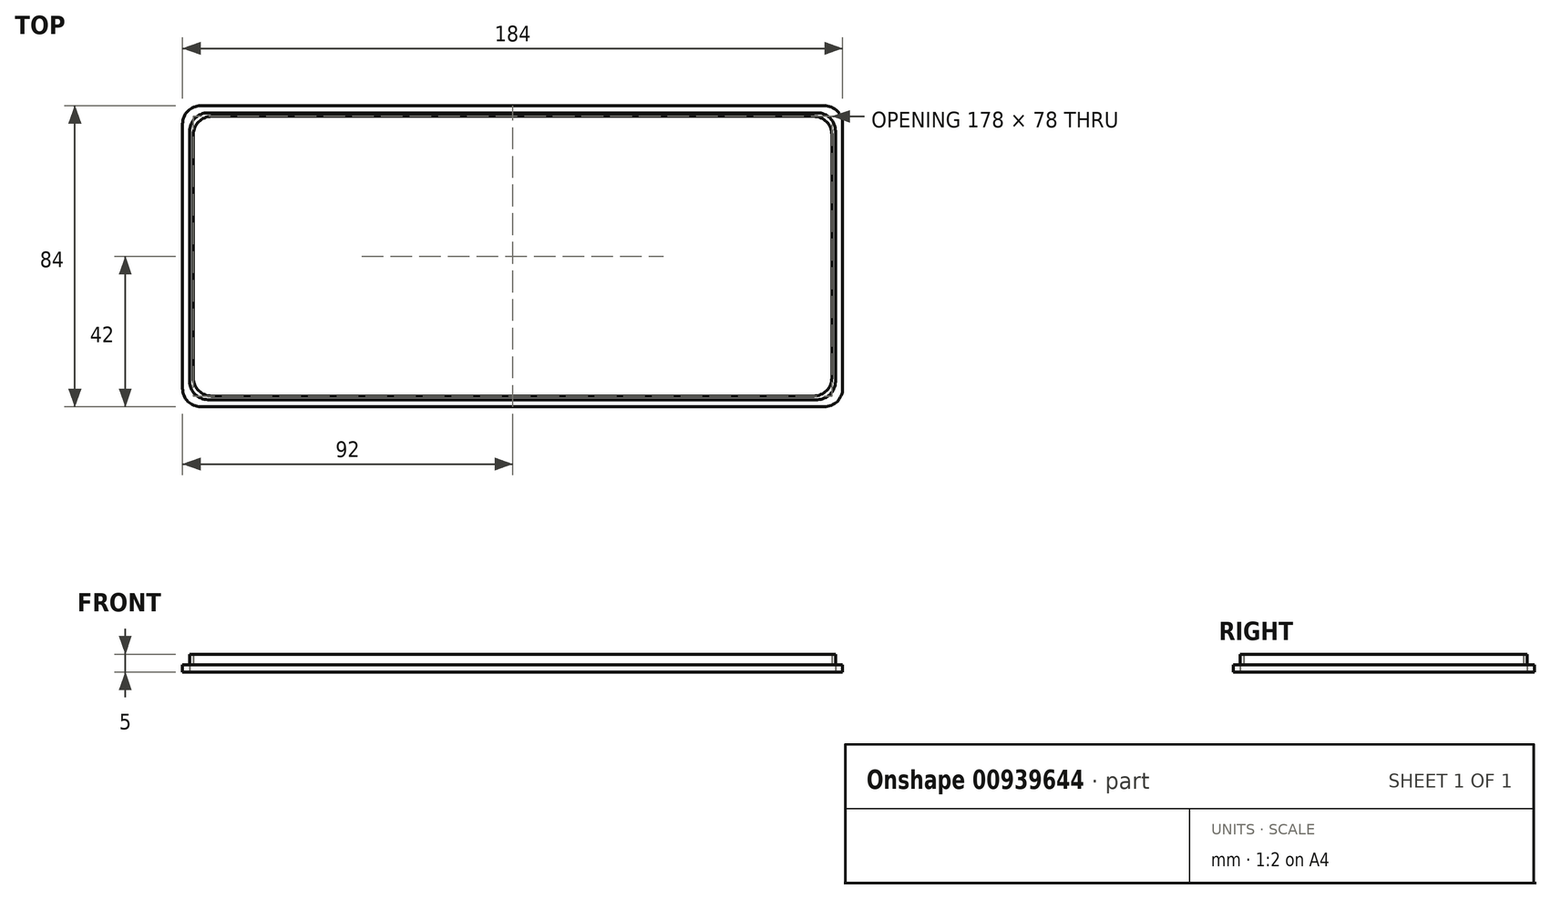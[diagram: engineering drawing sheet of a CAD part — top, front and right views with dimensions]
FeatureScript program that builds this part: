
annotation { "Feature Type Name" : "Feature", "Feature Type Description" : "" }
export const myFeature = defineFeature(function(context is Context, id is Id, definition is map)
    precondition{}
    {
        {
            var Q0;
            Q0=qCreatedBy(makeId("Top.planeOp"),FACE);
            var sketch = newSketch(context, id + "F0", { "sketchPlane" : qUnion([Q0])});
            skLineSegment(sketch, "E0.bottom", {"start": v(-90, 40) * mm, "end": v(90, 40) * mm});
            skLineSegment(sketch, "E0.top", {"start": v(-90, -40) * mm, "end": v(90, -40) * mm});
            skLineSegment(sketch, "E0.left", {"start": v(-90, 40) * mm, "end": v(-90, -40) * mm});
            skLineSegment(sketch, "E0.right", {"start": v(90, 40) * mm, "end": v(90, -40) * mm});
            skPoint(sketch, "E0.middle", {"position": v(0, 0) * mm});
            skLineSegment(sketch, "E1.0", {"start": v(-92, -42) * mm, "end": v(92, -42) * mm});
            skLineSegment(sketch, "E1.1", {"start": v(-92, 42) * mm, "end": v(-92, -42) * mm});
            skLineSegment(sketch, "E1.2", {"start": v(-92, 42) * mm, "end": v(92, 42) * mm});
            skLineSegment(sketch, "E1.3", {"start": v(92, 42) * mm, "end": v(92, -42) * mm});
            skLineSegment(sketch, "E2.bottom", {"start": v(-89, 39) * mm, "end": v(89, 39) * mm});
            skLineSegment(sketch, "E2.top", {"start": v(-89, -39) * mm, "end": v(89, -39) * mm});
            skLineSegment(sketch, "E2.left", {"start": v(-89, 39) * mm, "end": v(-89, -39) * mm});
            skLineSegment(sketch, "E2.right", {"start": v(89, 39) * mm, "end": v(89, -39) * mm});
            skSolve(sketch);
        }
        {
            var Q0;
            Q0=makeQuery(id+"F0.imprint","IMPRINT",FACE,{"disambiguationData":[TD([[makeQuery(id+"F0.imprint","IMPRINT",EDGE,{"derivedFrom":sQuery(id+"F0.wireOp",EDGE,"E0.bottom")}),1.0]])]});
            var Q1;
            Q1=makeQuery(id+"F0.imprint","IMPRINT",FACE,{"disambiguationData":[TD([[makeQuery(id+"F0.imprint","IMPRINT",EDGE,{"derivedFrom":sQuery(id+"F0.wireOp",EDGE,"E2.bottom")}),-1.0]])]});
            var Q2;
            Q2=makeQuery(id+"F0.imprint","IMPRINT",FACE,{"disambiguationData":[TD([[makeQuery(id+"F0.imprint","IMPRINT",EDGE,{"derivedFrom":sQuery(id+"F0.wireOp",EDGE,"E0.bottom")}),-1.0]])]});
            var Q3;
            Q3=sQuery(id+"F0.wireOp",EDGE,"E1.3");
            var Q4;
            Q4=sQuery(id+"F0.wireOp",EDGE,"E1.2");
            var Q5;
            Q5=sQuery(id+"F0.wireOp",EDGE,"E1.1");
            var Q6;
            Q6=sQuery(id+"F0.wireOp",EDGE,"E1.0");
            var Q7;
            Q7=sQuery(id+"F0.wireOp",EDGE,"E0.left");
            var Q8;
            Q8=sQuery(id+"F0.wireOp",EDGE,"E0.bottom");
            var Q9;
            Q9=sQuery(id+"F0.wireOp",EDGE,"E0.right");
            var Q10;
            Q10=sQuery(id+"F0.wireOp",EDGE,"E0.top");
            extrude(context, id + "F1", {"entities" : qUnion([Q0, Q1, Q2]), "surfaceEntities" : qUnion([Q3, Q4, Q5, Q6, Q7, Q8, Q9, Q10]), "depth" : 2 * mm, "offsetDistance" : 25.4 * mm});
        }
        {
            var Q0;
            Q0=makeQuery(id+"F0.imprint","IMPRINT",FACE,{"disambiguationData":[TD([[makeQuery(id+"F0.imprint","IMPRINT",EDGE,{"derivedFrom":sQuery(id+"F0.wireOp",EDGE,"E0.bottom")}),-1.0]])]});
            var Q1;
            Q1=sQuery(id+"F0.wireOp",EDGE,"E2.bottom");
            var Q2;
            Q2=sQuery(id+"F0.wireOp",EDGE,"E2.left");
            var Q3;
            Q3=sQuery(id+"F0.wireOp",EDGE,"E2.top");
            var Q4;
            Q4=sQuery(id+"F0.wireOp",EDGE,"E2.right");
            extrude(context, id + "F2", {"entities" : qUnion([Q0]), "surfaceEntities" : qUnion([Q1, Q2, Q3, Q4]), "depth" : 5 * mm, "offsetDistance" : 25.4 * mm});
        }
        {
            var Q0;
            Q0=makeQuery(id+"F2.opExtrude","SWEPT_EDGE",EDGE,{"disambiguationData":[OSD([sQuery(id+"F0.wireOp",EDGE,"E2.bottom"),sQuery(id+"F0.wireOp",EDGE,"E2.left")])]});
            var Q1;
            Q1=makeQuery(id+"F1.opExtrude","SWEPT_EDGE",EDGE,{"disambiguationData":[OSD([sQuery(id+"F0.wireOp",EDGE,"E1.1"),sQuery(id+"F0.wireOp",EDGE,"E1.2")])]});
            var Q2;
            Q2=makeQuery(id+"F2.opExtrude","SWEPT_EDGE",EDGE,{"disambiguationData":[OSD([sQuery(id+"F0.wireOp",EDGE,"E0.bottom"),sQuery(id+"F0.wireOp",EDGE,"E0.left")])]});
            var Q3;
            Q3=makeQuery(id+"F1.opExtrude","SWEPT_EDGE",EDGE,{"disambiguationData":[OSD([sQuery(id+"F0.wireOp",EDGE,"E1.0"),sQuery(id+"F0.wireOp",EDGE,"E1.1")])]});
            var Q4;
            Q4=makeQuery(id+"F2.opExtrude","SWEPT_EDGE",EDGE,{"disambiguationData":[OSD([sQuery(id+"F0.wireOp",EDGE,"E0.top"),sQuery(id+"F0.wireOp",EDGE,"E0.left")])]});
            var Q5;
            Q5=makeQuery(id+"F2.opExtrude","SWEPT_EDGE",EDGE,{"disambiguationData":[OSD([sQuery(id+"F0.wireOp",EDGE,"E2.top"),sQuery(id+"F0.wireOp",EDGE,"E2.left")])]});
            var Q6;
            Q6=makeQuery(id+"F1.opExtrude","SWEPT_EDGE",EDGE,{"disambiguationData":[OSD([sQuery(id+"F0.wireOp",EDGE,"E1.2"),sQuery(id+"F0.wireOp",EDGE,"E1.3")])]});
            var Q7;
            Q7=makeQuery(id+"F2.opExtrude","SWEPT_EDGE",EDGE,{"disambiguationData":[OSD([sQuery(id+"F0.wireOp",EDGE,"E0.bottom"),sQuery(id+"F0.wireOp",EDGE,"E0.right")])]});
            var Q8;
            Q8=makeQuery(id+"F2.opExtrude","SWEPT_EDGE",EDGE,{"disambiguationData":[OSD([sQuery(id+"F0.wireOp",EDGE,"E2.bottom"),sQuery(id+"F0.wireOp",EDGE,"E2.right")])]});
            var Q9;
            Q9=makeQuery(id+"F1.opExtrude","SWEPT_EDGE",EDGE,{"disambiguationData":[OSD([sQuery(id+"F0.wireOp",EDGE,"E1.0"),sQuery(id+"F0.wireOp",EDGE,"E1.3")])]});
            var Q10;
            Q10=makeQuery(id+"F2.opExtrude","SWEPT_EDGE",EDGE,{"disambiguationData":[OSD([sQuery(id+"F0.wireOp",EDGE,"E0.top"),sQuery(id+"F0.wireOp",EDGE,"E0.right")])]});
            var Q11;
            Q11=makeQuery(id+"F2.opExtrude","SWEPT_EDGE",EDGE,{"disambiguationData":[OSD([sQuery(id+"F0.wireOp",EDGE,"E2.top"),sQuery(id+"F0.wireOp",EDGE,"E2.right")])]});
            fillet(context, id + "F3", {"entities" : qUnion([Q0, Q1, Q2, Q3, Q4, Q5, Q6, Q7, Q8, Q9, Q10, Q11]), "radius" : 5.08 * mm, "tangentPropagation" : true, "allowEdgeOverflow" : false});
        }
    });
